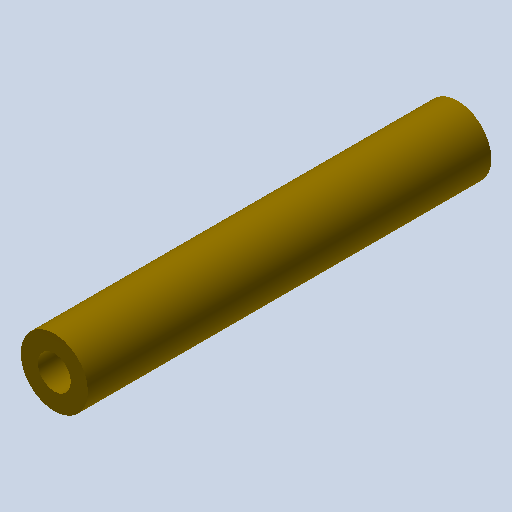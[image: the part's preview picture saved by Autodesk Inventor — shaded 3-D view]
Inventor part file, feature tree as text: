
AUTODESK INVENTOR PART (.ipt)
format: ipt  version: 2022.3 (Build 263350030, 350C)  size: 92,160 bytes
history: native  units: mm
features: sketch x2, extrude x1, hole x1
ambient origin geometry x8: Origin, YZ Plane, XZ Plane, XY Plane, X Axis, Y Axis, Z Axis, Center Point
bodies: Solid1 (feature_tree)
feature tree (4):
  extrude  "Extrusion1"  Depth=30.0mm TaperAngle=0.0deg
  hole  "Hole1"  [1 undecoded]
  sketch  "Sketch1"  dims[d0=5.0mm d1=30.0mm d2=0.0mm]
  sketch  "Sketch2"  dims[d3=2.459mm d4=10.0mm d5=4.0mm d6=2.0mm d7=90.0deg d8=8.0mm d9=20.594885mm]
note: 1 required parameter value undecoded (feature->parameter linkage not recoverable at this tier; creation-order binding heuristic only, values carry confidence <= 0.55)
